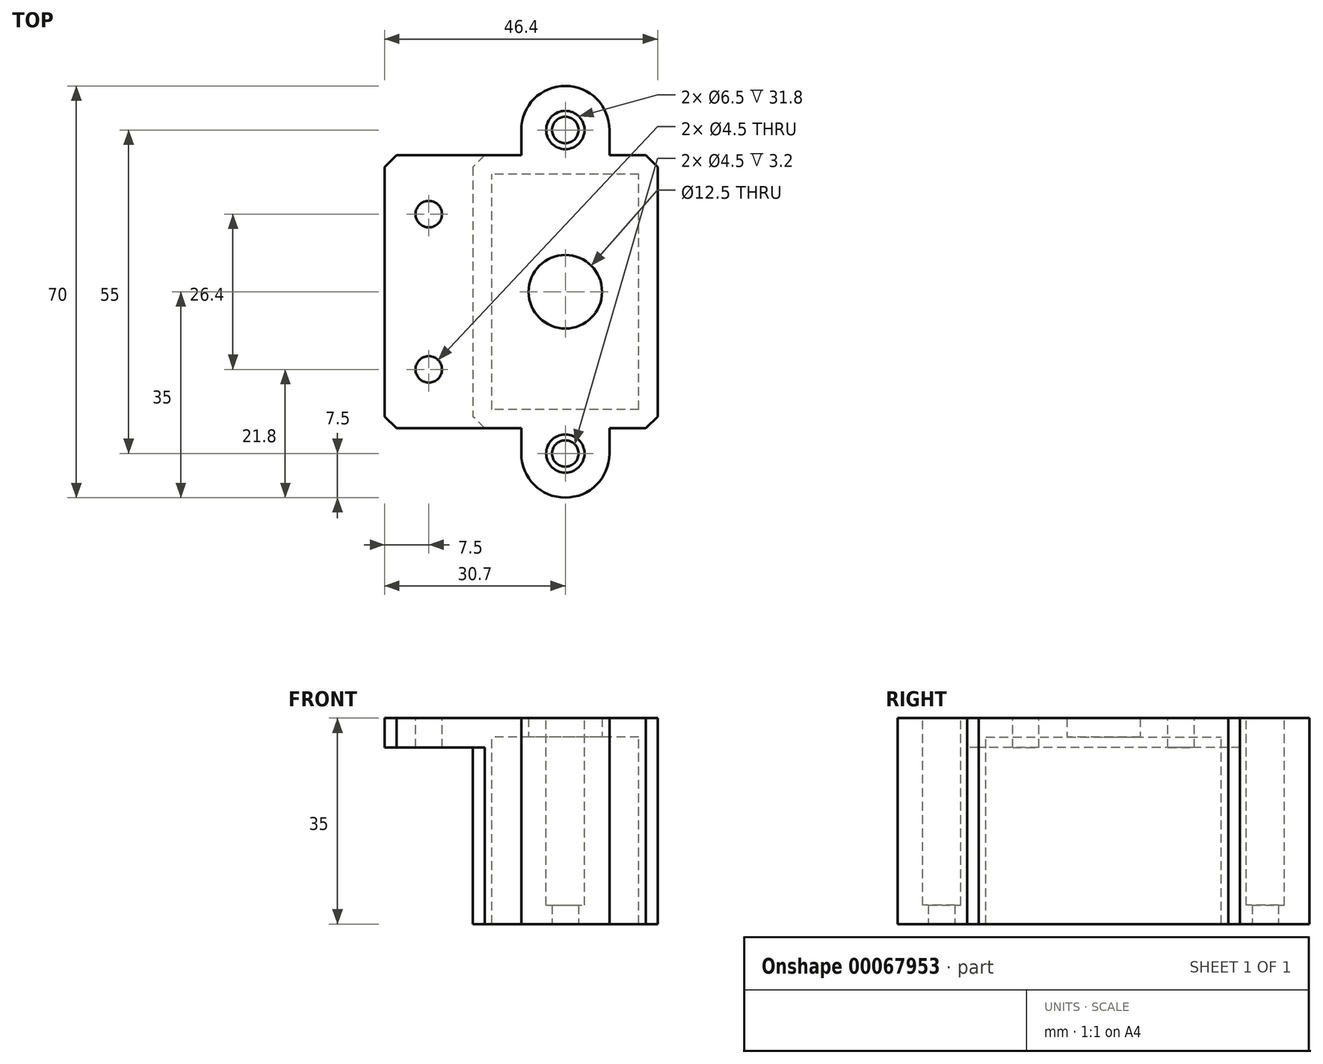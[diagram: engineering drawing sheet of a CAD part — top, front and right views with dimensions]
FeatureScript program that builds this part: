
annotation { "Feature Type Name" : "Feature", "Feature Type Description" : "" }
export const myFeature = defineFeature(function(context is Context, id is Id, definition is map)
    precondition{}
    {
        {
            var Q0;
            Q0=qCreatedBy(makeId("Top.planeOp"),FACE);
            var sketch = newSketch(context, id + "F0", { "sketchPlane" : qUnion([Q0])});
            skLineSegment(sketch, "E0.rect.bottom", {"start": v(12.5, -20) * mm, "end": v(-12.5, -20) * mm});
            skLineSegment(sketch, "E0.rect.top", {"start": v(12.5, 20) * mm, "end": v(-12.5, 20) * mm});
            skLineSegment(sketch, "E0.rect.left", {"start": v(12.5, -20) * mm, "end": v(12.5, 20) * mm});
            skLineSegment(sketch, "E0.rect.right", {"start": v(-12.5, -20) * mm, "end": v(-12.5, 20) * mm});
            skPoint(sketch, "E0.rect.middle", {"position": v(0, 0) * mm});
            skCircle(sketch, "E1", {"center": v(0, 0) * mm, "radius": 6.25 * mm});
            skSolve(sketch);
        }
        {
            var Q0;
            Q0 = qSketchRegion(id + "F0", true);
            extrude(context, id + "F1", {"entities" : qUnion([Q0]), "depth" : 3.2 * mm});
        }
        {
            var Q0;
            Q0=makeQuery(id+"F1.opExtrude","CAP_FACE",FACE,{"disambiguationData":[OSD([sQuery(id+"F0.wireOp",EDGE,"E0.rect.bottom"),sQuery(id+"F0.wireOp",EDGE,"E0.rect.top"),sQuery(id+"F0.wireOp",EDGE,"E0.rect.left"),sQuery(id+"F0.wireOp",EDGE,"E0.rect.right"),sQuery(id+"F0.wireOp",EDGE,"E1")])],"isStart":false});
            var sketch = newSketch(context, id + "F2", { "sketchPlane" : qUnion([Q0])});
            skLineSegment(sketch, "E2.rect.bottom", {"start": v(12.5, 20) * mm, "end": v(-12.5, 20) * mm});
            skLineSegment(sketch, "E2.rect.top", {"start": v(12.5, -20) * mm, "end": v(-12.5, -20) * mm});
            skLineSegment(sketch, "E2.rect.left", {"start": v(12.5, 20) * mm, "end": v(12.5, -20) * mm});
            skLineSegment(sketch, "E2.rect.right", {"start": v(-12.5, 20) * mm, "end": v(-12.5, -20) * mm});
            skPoint(sketch, "E2.rect.middle", {"position": v(0, 0) * mm});
            skLineSegment(sketch, "E3.rect.bottom", {"start": v(15.7, 23.2) * mm, "end": v(7.5, 23.2) * mm});
            skLineSegment(sketch, "E3.rect.left", {"start": v(15.7, 23.2) * mm, "end": v(15.7, -23.2) * mm});
            skLineSegment(sketch, "E3.rect.right", {"start": v(-15.7, 23.2) * mm, "end": v(-15.7, -23.2) * mm});
            skLineSegment(sketch, "E4", {"start": v(-7.5, 23.2) * mm, "end": v(-7.5, 27.5) * mm});
            skLineSegment(sketch, "E5", {"start": v(0, 27.5) * mm, "end": v(0, 23.2) * mm});
            skLineSegment(sketch, "E6", {"start": v(0, 0) * mm, "end": v(-6.25, 0) * mm, "construction": true});
            skLineSegment(sketch, "E7.MirrorCS", {"start": v(7.5, 23.2) * mm, "end": v(7.5, 27.5) * mm});
            skArc(sketch, "E8", {"start": v(-7.5, 27.5) * mm, "mid": v(0, 35) * mm, "end": v(7.5, 27.5) * mm});
            skLineSegment(sketch, "E9.MirrorCS", {"start": v(-7.5, -23.2) * mm, "end": v(-7.5, -27.5) * mm});
            skLineSegment(sketch, "E10.MirrorCS", {"start": v(15.7, -23.2) * mm, "end": v(7.5, -23.2) * mm});
            skLineSegment(sketch, "E11.MirrorCS", {"start": v(0, -27.5) * mm, "end": v(0, -23.2) * mm, "construction": true});
            skArc(sketch, "E12.MirrorCS", {"start": v(-7.5, -27.5) * mm, "mid": v(0, -35) * mm, "end": v(7.5, -27.5) * mm});
            skLineSegment(sketch, "E13.MirrorCS", {"start": v(7.5, -23.2) * mm, "end": v(7.5, -27.5) * mm});
            skLineSegment(sketch, "E14.trimOffspring", {"start": v(-7.5, -23.2) * mm, "end": v(-15.7, -23.2) * mm});
            skLineSegment(sketch, "E15.trimOffspring", {"start": v(-7.5, 23.2) * mm, "end": v(-15.7, 23.2) * mm});
            skCircle(sketch, "E16.cCircle", {"center": v(0, 27.5) * mm, "radius": 2.98 * mm, "construction": true});
            skLineSegment(sketch, "E16.0", {"start": v(-1.72, 30.48) * mm, "end": v(1.72, 30.48) * mm, "construction": true});
            skLineSegment(sketch, "E16.1", {"start": v(1.72, 30.48) * mm, "end": v(3.44, 27.5) * mm, "construction": true});
            skLineSegment(sketch, "E16.2", {"start": v(3.44, 27.5) * mm, "end": v(1.72, 24.52) * mm, "construction": true});
            skLineSegment(sketch, "E16.3", {"start": v(1.72, 24.52) * mm, "end": v(-1.72, 24.52) * mm, "construction": true});
            skLineSegment(sketch, "E16.4", {"start": v(-1.72, 24.52) * mm, "end": v(-3.44, 27.5) * mm, "construction": true});
            skLineSegment(sketch, "E16.5", {"start": v(-3.44, 27.5) * mm, "end": v(-1.72, 30.48) * mm, "construction": true});
            skPoint(sketch, "E16.0.midPoint", {"position": v(0, 30.48) * mm});
            skCircle(sketch, "E17.cCircle", {"center": v(0, -27.5) * mm, "radius": 2.98 * mm, "construction": true});
            skLineSegment(sketch, "E17.0", {"start": v(-1.72, -24.52) * mm, "end": v(1.72, -24.52) * mm, "construction": true});
            skLineSegment(sketch, "E17.1", {"start": v(1.72, -24.52) * mm, "end": v(3.44, -27.5) * mm, "construction": true});
            skLineSegment(sketch, "E17.2", {"start": v(3.44, -27.5) * mm, "end": v(1.72, -30.47) * mm, "construction": true});
            skLineSegment(sketch, "E17.3", {"start": v(1.72, -30.48) * mm, "end": v(-1.72, -30.48) * mm, "construction": true});
            skLineSegment(sketch, "E17.4", {"start": v(-1.72, -30.48) * mm, "end": v(-3.44, -27.5) * mm, "construction": true});
            skLineSegment(sketch, "E17.5", {"start": v(-3.44, -27.5) * mm, "end": v(-1.72, -24.52) * mm, "construction": true});
            skPoint(sketch, "E17.0.midPoint", {"position": v(0, -24.52) * mm});
            skCircle(sketch, "E18", {"center": v(0, -27.5) * mm, "radius": 3.25 * mm});
            skCircle(sketch, "E19", {"center": v(0, 27.5) * mm, "radius": 3.25 * mm});
            skSolve(sketch);
        }
        {
            var Q0;
            Q0 = qSketchRegion(id + "F2", true);
            extrude(context, id + "F3", {"entities" : qUnion([Q0]), "operationType" : NewBodyOperationType.ADD, "oppositeDirection" : true, "depth" : 35 * mm});
        }
        {
            var Q0;
            Q0=makeQuery(id+"F3.boolean.opBoolean","MERGE",FACE,{"derivedFrom":[makeQuery(id+"F1.opExtrude","CAP_FACE",FACE,{"disambiguationData":[OSD([sQuery(id+"F0.wireOp",EDGE,"E0.rect.bottom"),sQuery(id+"F0.wireOp",EDGE,"E0.rect.top"),sQuery(id+"F0.wireOp",EDGE,"E0.rect.left"),sQuery(id+"F0.wireOp",EDGE,"E0.rect.right"),sQuery(id+"F0.wireOp",EDGE,"E1")])],"isStart":false}),makeQuery(id+"F3.opExtrude","CAP_FACE",FACE,{"disambiguationData":[OSD([sQuery(id+"F2.wireOp",EDGE,"E2.rect.bottom"),sQuery(id+"F2.wireOp",EDGE,"E2.rect.top"),sQuery(id+"F2.wireOp",EDGE,"E2.rect.left"),sQuery(id+"F2.wireOp",EDGE,"E2.rect.right"),sQuery(id+"F2.wireOp",EDGE,"E3.rect.bottom"),sQuery(id+"F2.wireOp",EDGE,"E3.rect.top"),sQuery(id+"F2.wireOp",EDGE,"E3.rect.left"),sQuery(id+"F2.wireOp",EDGE,"E3.rect.right")])],"isStart":true})]});
            var sketch = newSketch(context, id + "F4", { "sketchPlane" : qUnion([Q0])});
            skLineSegment(sketch, "E20", {"start": v(-15.7, 23.2) * mm, "end": v(-30.7, 23.2) * mm});
            skLineSegment(sketch, "E21", {"start": v(-30.7, 23.2) * mm, "end": v(-30.7, -23.2) * mm});
            skLineSegment(sketch, "E22", {"start": v(-30.7, -23.2) * mm, "end": v(-15.7, -23.2) * mm});
            skLineSegment(sketch, "E23", {"start": v(-15.7, -23.2) * mm, "end": v(-15.7, 23.2) * mm});
            skCircle(sketch, "E24", {"center": v(-23.2, 13.2) * mm, "radius": 2.25 * mm});
            skCircle(sketch, "E25", {"center": v(-23.2, -13.2) * mm, "radius": 2.25 * mm});
            skPoint(sketch, "E25.centerSnap0", {"position": v(-23.2, -23.2) * mm});
            skSolve(sketch);
        }
        {
            var Q0;
            Q0 = qSketchRegion(id + "F4", true);
            extrude(context, id + "F5", {"entities" : qUnion([Q0]), "operationType" : NewBodyOperationType.ADD, "oppositeDirection" : true, "depth" : 5 * mm});
        }
        {
            var Q0;
            Q0=makeQuery(id+"F3.opExtrude","SWEPT_EDGE",EDGE,{"disambiguationData":[OSD([sQuery(id+"F2.wireOp",EDGE,"E3.rect.bottom"),sQuery(id+"F2.wireOp",EDGE,"E3.rect.left")])]});
            var Q1;
            Q1=makeQuery(id+"F3.opExtrude","SWEPT_EDGE",EDGE,{"disambiguationData":[OSD([sQuery(id+"F2.wireOp",EDGE,"E3.rect.right"),sQuery(id+"F2.wireOp",EDGE,"E15.trimOffspring")])]});
            var Q2;
            Q2=makeQuery(id+"F3.opExtrude","SWEPT_EDGE",EDGE,{"disambiguationData":[OSD([sQuery(id+"F2.wireOp",EDGE,"E3.rect.right"),sQuery(id+"F2.wireOp",EDGE,"E14.trimOffspring")])]});
            var Q3;
            Q3=makeQuery(id+"F3.opExtrude","SWEPT_EDGE",EDGE,{"disambiguationData":[OSD([sQuery(id+"F2.wireOp",EDGE,"E3.rect.bottom"),sQuery(id+"F2.wireOp",EDGE,"E3.rect.left")])]});
            var Q4;
            Q4=makeQuery(id+"F3.opExtrude","SWEPT_EDGE",EDGE,{"disambiguationData":[OSD([sQuery(id+"F2.wireOp",EDGE,"E3.rect.bottom"),sQuery(id+"F2.wireOp",EDGE,"E3.rect.left")])]});
            var Q5;
            Q5=makeQuery(id+"F3.opExtrude","SWEPT_EDGE",EDGE,{"disambiguationData":[OSD([sQuery(id+"F2.wireOp",EDGE,"E3.rect.left"),sQuery(id+"F2.wireOp",EDGE,"E10.MirrorCS")])]});
            var Q6;
            Q6=makeQuery(id+"F3.opExtrude","SWEPT_EDGE",EDGE,{"disambiguationData":[OSD([sQuery(id+"F2.wireOp",EDGE,"E3.rect.right"),sQuery(id+"F2.wireOp",EDGE,"E15.trimOffspring")])]});
            var Q7;
            Q7=makeQuery(id+"F3.opExtrude","SWEPT_EDGE",EDGE,{"disambiguationData":[OSD([sQuery(id+"F2.wireOp",EDGE,"E3.rect.right"),sQuery(id+"F2.wireOp",EDGE,"E14.trimOffspring")])]});
            var Q8;
            Q8=makeQuery(id+"F5.opExtrude","SWEPT_EDGE",EDGE,{"disambiguationData":[OSD([sQuery(id+"F4.wireOp",EDGE,"E20"),sQuery(id+"F4.wireOp",EDGE,"E21")])]});
            var Q9;
            Q9=makeQuery(id+"F5.opExtrude","SWEPT_EDGE",EDGE,{"disambiguationData":[OSD([sQuery(id+"F4.wireOp",EDGE,"E21"),sQuery(id+"F4.wireOp",EDGE,"E22")])]});
            chamfer(context, id + "F6", {"entities" : qUnion([Q0, Q1, Q2, Q3, Q4, Q5, Q6, Q7, Q8, Q9]), "width" : 2 * mm, "tangentPropagation" : true});
        }
        {
            var Q0;
            Q0=makeQuery(id+"F3.opExtrude","CAP_FACE",FACE,{"disambiguationData":[OSD([sQuery(id+"F2.wireOp",EDGE,"E2.rect.bottom"),sQuery(id+"F2.wireOp",EDGE,"E2.rect.top"),sQuery(id+"F2.wireOp",EDGE,"E2.rect.left"),sQuery(id+"F2.wireOp",EDGE,"E2.rect.right"),sQuery(id+"F2.wireOp",EDGE,"E3.rect.bottom"),sQuery(id+"F2.wireOp",EDGE,"E3.rect.left"),sQuery(id+"F2.wireOp",EDGE,"E3.rect.right"),sQuery(id+"F2.wireOp",EDGE,"E4"),sQuery(id+"F2.wireOp",EDGE,"E7.MirrorCS"),sQuery(id+"F2.wireOp",EDGE,"E8"),sQuery(id+"F2.wireOp",EDGE,"E9.MirrorCS"),sQuery(id+"F2.wireOp",EDGE,"E10.MirrorCS"),sQuery(id+"F2.wireOp",EDGE,"E12.MirrorCS"),sQuery(id+"F2.wireOp",EDGE,"E13.MirrorCS"),sQuery(id+"F2.wireOp",EDGE,"E14.trimOffspring"),sQuery(id+"F2.wireOp",EDGE,"E15.trimOffspring"),sQuery(id+"F2.wireOp",EDGE,"E16.0"),sQuery(id+"F2.wireOp",EDGE,"E16.1"),sQuery(id+"F2.wireOp",EDGE,"E16.2"),sQuery(id+"F2.wireOp",EDGE,"E16.3"),sQuery(id+"F2.wireOp",EDGE,"E16.4"),sQuery(id+"F2.wireOp",EDGE,"E16.5"),sQuery(id+"F2.wireOp",EDGE,"E17.0"),sQuery(id+"F2.wireOp",EDGE,"E17.1"),sQuery(id+"F2.wireOp",EDGE,"E17.2"),sQuery(id+"F2.wireOp",EDGE,"E17.3"),sQuery(id+"F2.wireOp",EDGE,"E17.4"),sQuery(id+"F2.wireOp",EDGE,"E17.5")])],"isStart":false});
            var sketch = newSketch(context, id + "F7", { "sketchPlane" : qUnion([Q0])});
            skLineSegment(sketch, "E26", {"start": v(0, 0) * mm, "end": v(12.5, 0) * mm, "construction": true});
            skCircle(sketch, "E27", {"center": v(0, 27.5) * mm, "radius": 2.25 * mm});
            skCircle(sketch, "E28.MirrorC", {"center": v(0, -27.5) * mm, "radius": 3.25 * mm, "construction": true});
            skCircle(sketch, "E29.MirrorC", {"center": v(0, -27.5) * mm, "radius": 2.25 * mm});
            skCircle(sketch, "E30", {"center": v(0, -27.5) * mm, "radius": 3.25 * mm});
            skCircle(sketch, "E31", {"center": v(0, 27.5) * mm, "radius": 3.25 * mm});
            skSolve(sketch);
        }
        {
            var Q0;
            Q0 = qSketchRegion(id + "F7", true);
            extrude(context, id + "F8", {"entities" : qUnion([Q0]), "operationType" : NewBodyOperationType.ADD, "oppositeDirection" : true, "depth" : 3.2 * mm});
        }
    });
